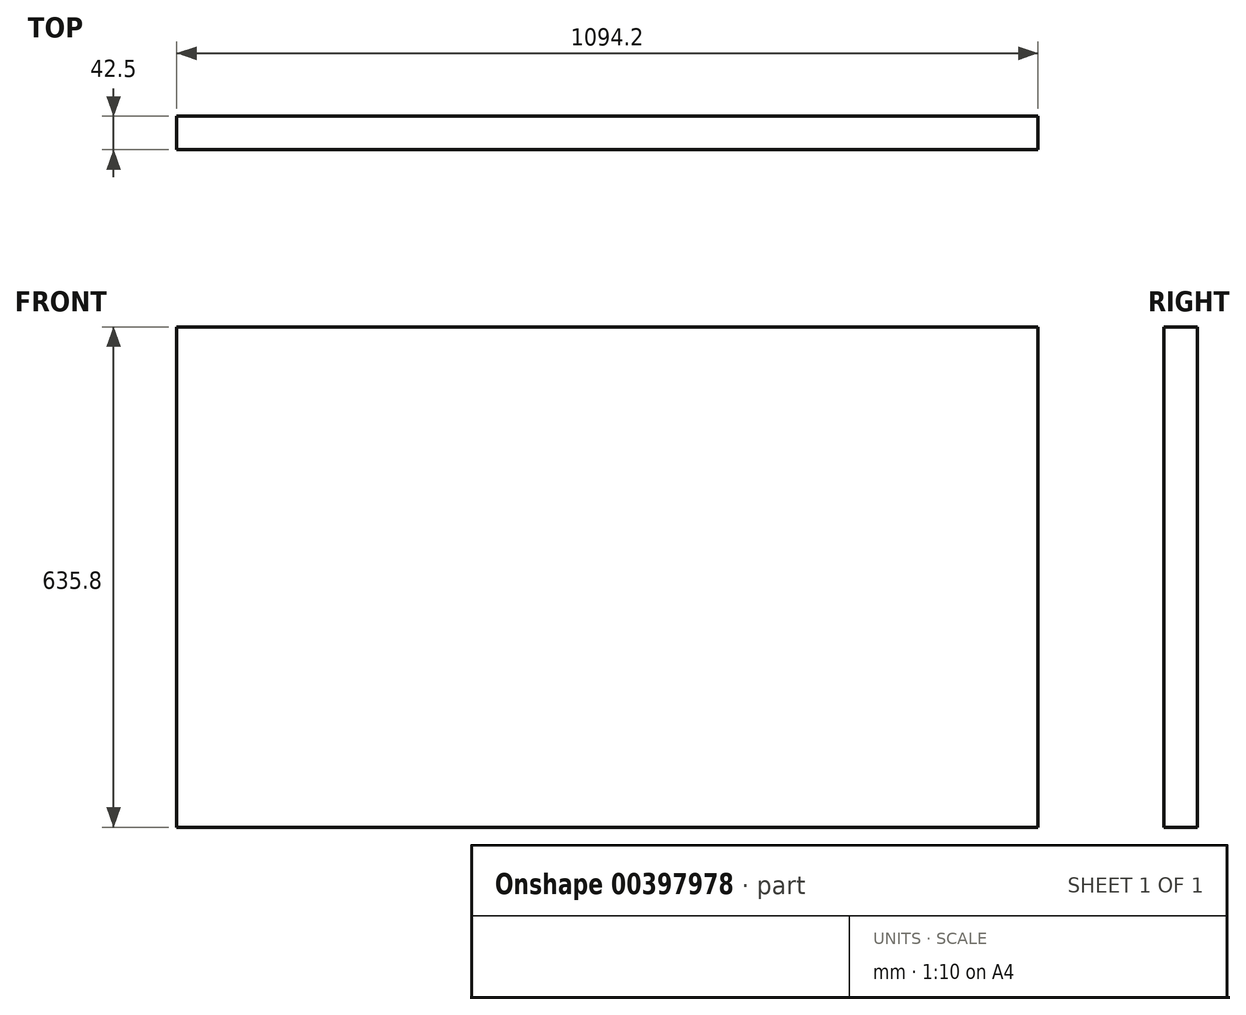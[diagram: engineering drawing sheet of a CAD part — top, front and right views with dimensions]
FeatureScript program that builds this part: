
annotation { "Feature Type Name" : "Feature", "Feature Type Description" : "" }
export const myFeature = defineFeature(function(context is Context, id is Id, definition is map)
    precondition{}
    {
        {
            var Q0;
            Q0=qCreatedBy(makeId("Front.planeOp"),FACE);
            var sketch = newSketch(context, id + "F0", { "sketchPlane" : qUnion([Q0])});
            skLineSegment(sketch, "E0.bottom", {"start": v(-545.41, -351.04) * mm, "end": v(548.79, -351.04) * mm});
            skLineSegment(sketch, "E0.top", {"start": v(-545.41, 284.76) * mm, "end": v(548.79, 284.76) * mm});
            skLineSegment(sketch, "E0.left", {"start": v(-545.41, -351.04) * mm, "end": v(-545.41, 284.76) * mm});
            skLineSegment(sketch, "E0.right", {"start": v(548.79, -351.04) * mm, "end": v(548.79, 284.76) * mm});
            skSolve(sketch);
        }
        {
            var Q0;
            Q0=makeQuery(id+"F0.imprint","IMPRINT",FACE,{"disambiguationData":[TD([[makeQuery(id+"F0.imprint","IMPRINT",EDGE,{"derivedFrom":sQuery(id+"F0.wireOp",EDGE,"E0.bottom")}),1.0]])]});
            extrude(context, id + "F1", {"entities" : qUnion([Q0]), "depth" : 42.5 * mm});
        }
    });
